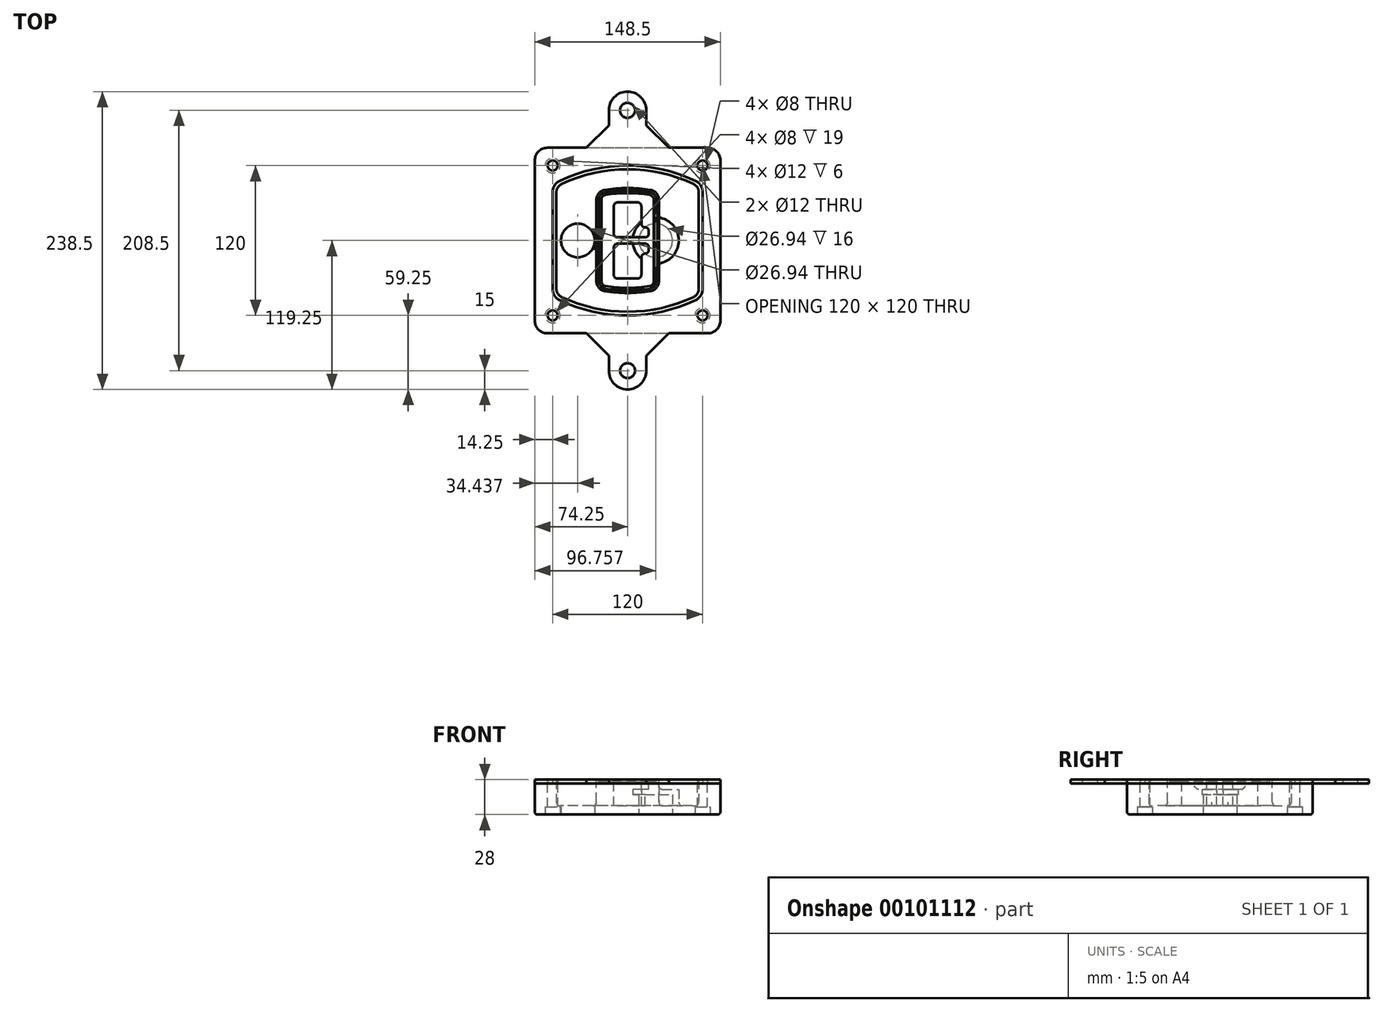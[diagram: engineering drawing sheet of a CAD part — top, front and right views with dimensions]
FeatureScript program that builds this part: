
annotation { "Feature Type Name" : "Feature", "Feature Type Description" : "" }
export const myFeature = defineFeature(function(context is Context, id is Id, definition is map)
    precondition{}
    {
        {
            var Q0;
            Q0=qCreatedBy(makeId("Top.planeOp"),FACE);
            var sketch = newSketch(context, id + "F0", { "sketchPlane" : qUnion([Q0])});
            skPoint(sketch, "E0.rect.middle", {"position": v(0, 0) * mm});
            skLineSegment(sketch, "E1.bottom", {"start": v(-64.25, -74.25) * mm, "end": v(64.25, -74.25) * mm});
            skLineSegment(sketch, "E1.top", {"start": v(-64.25, 74.25) * mm, "end": v(64.25, 74.25) * mm});
            skLineSegment(sketch, "E1.left", {"start": v(-74.25, -64.25) * mm, "end": v(-74.25, 64.25) * mm});
            skLineSegment(sketch, "E1.right", {"start": v(74.25, -64.25) * mm, "end": v(74.25, 64.25) * mm});
            skLineSegment(sketch, "E2", {"start": v(-74.25, 74.25) * mm, "end": v(74.25, -74.25) * mm, "construction": true});
            skLineSegment(sketch, "E3", {"start": v(74.25, 74.25) * mm, "end": v(-74.25, -74.25) * mm, "construction": true});
            skCircle(sketch, "E4", {"center": v(-60, 60) * mm, "radius": 4 * mm});
            skCircle(sketch, "E5", {"center": v(60, 60) * mm, "radius": 4 * mm});
            skCircle(sketch, "E6", {"center": v(60, -60) * mm, "radius": 4 * mm});
            skCircle(sketch, "E7", {"center": v(-60, -60) * mm, "radius": 4 * mm});
            skLineSegment(sketch, "E8", {"start": v(-60, 60) * mm, "end": v(60, 60) * mm, "construction": true});
            skLineSegment(sketch, "E9", {"start": v(60, 60) * mm, "end": v(60, -60) * mm, "construction": true});
            skLineSegment(sketch, "E10", {"start": v(60, -60) * mm, "end": v(-60, -60) * mm, "construction": true});
            skLineSegment(sketch, "E11", {"start": v(-60, -60) * mm, "end": v(-60, 60) * mm, "construction": true});
            skLineSegment(sketch, "E12", {"start": v(-60, 38.83) * mm, "end": v(-60, -38.83) * mm});
            skLineSegment(sketch, "E13", {"start": v(60, 38.83) * mm, "end": v(60, -38.83) * mm});
            skArc(sketch, "E14", {"start": v(54.26, 47.88) * mm, "mid": v(0, 60) * mm, "end": v(-54.26, 47.88) * mm});
            skArc(sketch, "E15", {"start": v(-54.26, -47.88) * mm, "mid": v(0, -60) * mm, "end": v(54.26, -47.88) * mm});
            skLineSegment(sketch, "E16", {"start": v(-60, 0) * mm, "end": v(60, 0) * mm, "construction": true});
            skPoint(sketch, "E17.visualSharp", {"position": v(-60, -45) * mm});
            skArc(sketch, "E17.filletArc", {"start": v(-60, -38.83) * mm, "mid": v(-58.44, -44.2) * mm, "end": v(-54.26, -47.88) * mm});
            skPoint(sketch, "E18.visualSharp", {"position": v(-60, 45) * mm});
            skArc(sketch, "E18.filletArc", {"start": v(-54.26, 47.88) * mm, "mid": v(-58.44, 44.2) * mm, "end": v(-60, 38.83) * mm});
            skPoint(sketch, "E19.visualSharp", {"position": v(60, 45) * mm});
            skArc(sketch, "E19.filletArc", {"start": v(60, 38.83) * mm, "mid": v(58.44, 44.2) * mm, "end": v(54.26, 47.88) * mm});
            skPoint(sketch, "E20.visualSharp", {"position": v(60, -45) * mm});
            skArc(sketch, "E20.filletArc", {"start": v(54.26, -47.88) * mm, "mid": v(58.44, -44.2) * mm, "end": v(60, -38.83) * mm});
            skPoint(sketch, "E21.visualSharp", {"position": v(-74.25, 74.25) * mm});
            skArc(sketch, "E21.filletArc", {"start": v(-64.25, 74.25) * mm, "mid": v(-71.32, 71.32) * mm, "end": v(-74.25, 64.25) * mm});
            skPoint(sketch, "E22.visualSharp", {"position": v(74.25, 74.25) * mm});
            skArc(sketch, "E22.filletArc", {"start": v(74.25, 64.25) * mm, "mid": v(71.32, 71.32) * mm, "end": v(64.25, 74.25) * mm});
            skPoint(sketch, "E23.visualSharp", {"position": v(74.25, -74.25) * mm});
            skArc(sketch, "E23.filletArc", {"start": v(64.25, -74.25) * mm, "mid": v(71.32, -71.32) * mm, "end": v(74.25, -64.25) * mm});
            skPoint(sketch, "E24.visualSharp", {"position": v(-74.25, -74.25) * mm});
            skArc(sketch, "E24.filletArc", {"start": v(-74.25, -64.25) * mm, "mid": v(-71.32, -71.32) * mm, "end": v(-64.25, -74.25) * mm});
            skArc(sketch, "E25.0", {"start": v(57, 38.83) * mm, "mid": v(55.9, 42.58) * mm, "end": v(52.98, 45.17) * mm});
            skLineSegment(sketch, "E25.1", {"start": v(57, 38.83) * mm, "end": v(57, -38.83) * mm});
            skArc(sketch, "E25.2", {"start": v(52.98, -45.17) * mm, "mid": v(55.9, -42.58) * mm, "end": v(57, -38.83) * mm});
            skArc(sketch, "E25.3", {"start": v(-52.98, -45.17) * mm, "mid": v(0, -57) * mm, "end": v(52.98, -45.17) * mm});
            skArc(sketch, "E25.4", {"start": v(-57, -38.83) * mm, "mid": v(-55.9, -42.58) * mm, "end": v(-52.98, -45.17) * mm});
            skArc(sketch, "E25.5", {"start": v(52.98, 45.17) * mm, "mid": v(0, 57) * mm, "end": v(-52.98, 45.17) * mm});
            skLineSegment(sketch, "E25.6", {"start": v(-57, 38.83) * mm, "end": v(-57, -38.83) * mm});
            skArc(sketch, "E25.7", {"start": v(-52.98, 45.17) * mm, "mid": v(-55.9, 42.58) * mm, "end": v(-57, 38.83) * mm});
            skArc(sketch, "E26.0", {"start": v(-55.96, 51.5) * mm, "mid": v(-61.82, 46.33) * mm, "end": v(-64, 38.83) * mm});
            skArc(sketch, "E26.1", {"start": v(55.96, 51.5) * mm, "mid": v(0, 64) * mm, "end": v(-55.96, 51.5) * mm});
            skArc(sketch, "E26.2", {"start": v(64, 38.83) * mm, "mid": v(61.82, 46.33) * mm, "end": v(55.96, 51.5) * mm});
            skLineSegment(sketch, "E26.3", {"start": v(64, 38.83) * mm, "end": v(64, -38.83) * mm});
            skArc(sketch, "E26.4", {"start": v(55.96, -51.5) * mm, "mid": v(61.82, -46.33) * mm, "end": v(64, -38.83) * mm});
            skLineSegment(sketch, "E26.5", {"start": v(-64, 38.83) * mm, "end": v(-64, -38.83) * mm});
            skArc(sketch, "E26.6", {"start": v(-55.96, -51.5) * mm, "mid": v(0, -64) * mm, "end": v(55.96, -51.5) * mm});
            skArc(sketch, "E26.7", {"start": v(-64, -38.83) * mm, "mid": v(-61.82, -46.33) * mm, "end": v(-55.96, -51.5) * mm});
            skSolve(sketch);
        }
        {
            var Q0;
            Q0=makeQuery(id+"F0.imprint","IMPRINT",FACE,{"disambiguationData":[TD([[makeQuery(id+"F0.imprint","IMPRINT",EDGE,{"derivedFrom":sQuery(id+"F0.wireOp",EDGE,"E1.bottom")}),1.0]])]});
            var Q1;
            Q1=makeQuery(id+"F0.imprint","IMPRINT",FACE,{"disambiguationData":[TD([[makeQuery(id+"F0.imprint","IMPRINT",EDGE,{"derivedFrom":sQuery(id+"F0.wireOp",EDGE,"E12")}),1.0]])]});
            var Q2;
            Q2=makeQuery(id+"F0.imprint","IMPRINT",FACE,{"disambiguationData":[TD([[makeQuery(id+"F0.imprint","IMPRINT",EDGE,{"derivedFrom":sQuery(id+"F0.wireOp",EDGE,"E25.0")}),1.0]])]});
            var Q3;
            Q3=makeQuery(id+"F0.imprint","IMPRINT",FACE,{"disambiguationData":[TD([[makeQuery(id+"F0.imprint","IMPRINT",EDGE,{"derivedFrom":sQuery(id+"F0.wireOp",EDGE,"E12")}),-1.0]])]});
            extrude(context, id + "F1", {"entities" : qUnion([Q0, Q1, Q2, Q3]), "oppositeDirection" : true, "depth" : 25 * mm});
        }
        {
            var Q0;
            Q0=makeQuery(id+"F0.imprint","IMPRINT",FACE,{"disambiguationData":[TD([[makeQuery(id+"F0.imprint","IMPRINT",EDGE,{"derivedFrom":sQuery(id+"F0.wireOp",EDGE,"E12")}),1.0]])]});
            extrude(context, id + "F2", {"entities" : qUnion([Q0]), "operationType" : NewBodyOperationType.ADD, "depth" : 3 * mm});
        }
        {
            var Q0;
            Q0=makeQuery(id+"F0.imprint","IMPRINT",FACE,{"disambiguationData":[TD([[makeQuery(id+"F0.imprint","IMPRINT",EDGE,{"derivedFrom":sQuery(id+"F0.wireOp",EDGE,"E25.0")}),1.0]])]});
            extrude(context, id + "F3", {"entities" : qUnion([Q0]), "operationType" : NewBodyOperationType.REMOVE, "oppositeDirection" : true, "depth" : 18 * mm});
        }
        {
            var Q0;
            Q0=makeQuery(id+"F2.opExtrude","CAP_FACE",FACE,{"disambiguationData":[OSD([sQuery(id+"F0.wireOp",EDGE,"E12"),sQuery(id+"F0.wireOp",EDGE,"E13"),sQuery(id+"F0.wireOp",EDGE,"E14"),sQuery(id+"F0.wireOp",EDGE,"E15"),sQuery(id+"F0.wireOp",EDGE,"E17.filletArc"),sQuery(id+"F0.wireOp",EDGE,"E18.filletArc"),sQuery(id+"F0.wireOp",EDGE,"E19.filletArc"),sQuery(id+"F0.wireOp",EDGE,"E20.filletArc"),sQuery(id+"F0.wireOp",EDGE,"E25.0"),sQuery(id+"F0.wireOp",EDGE,"E25.1"),sQuery(id+"F0.wireOp",EDGE,"E25.2"),sQuery(id+"F0.wireOp",EDGE,"E25.3"),sQuery(id+"F0.wireOp",EDGE,"E25.4"),sQuery(id+"F0.wireOp",EDGE,"E25.5"),sQuery(id+"F0.wireOp",EDGE,"E25.6"),sQuery(id+"F0.wireOp",EDGE,"E25.7")])],"isStart":false});
            var sketch = newSketch(context, id + "F4", { "sketchPlane" : qUnion([Q0])});
            skArc(sketch, "E27.0", {"start": v(-18.34, -40.45) * mm, "mid": v(0, -42) * mm, "end": v(18.34, -40.45) * mm});
            skArc(sketch, "E28.0", {"start": v(18.34, 40.45) * mm, "mid": v(0, 42) * mm, "end": v(-18.34, 40.45) * mm});
            skLineSegment(sketch, "E29", {"start": v(-25, 32.57) * mm, "end": v(-25, -32.57) * mm});
            skLineSegment(sketch, "E30", {"start": v(25, 32.57) * mm, "end": v(25, -32.57) * mm});
            skLineSegment(sketch, "E31", {"start": v(-25, 39.1) * mm, "end": v(25, 39.1) * mm, "construction": true});
            skLineSegment(sketch, "E32", {"start": v(-25, -39.1) * mm, "end": v(25, -39.1) * mm, "construction": true});
            skPoint(sketch, "E33.visualSharp", {"position": v(-25, 39.1) * mm});
            skArc(sketch, "E33.filletArc", {"start": v(-18.34, 40.45) * mm, "mid": v(-23.11, 37.73) * mm, "end": v(-25, 32.57) * mm});
            skPoint(sketch, "E34.visualSharp", {"position": v(25, 39.1) * mm});
            skArc(sketch, "E34.filletArc", {"start": v(25, 32.57) * mm, "mid": v(23.11, 37.73) * mm, "end": v(18.34, 40.45) * mm});
            skPoint(sketch, "E35.visualSharp", {"position": v(25, -39.1) * mm});
            skArc(sketch, "E35.filletArc", {"start": v(18.34, -40.45) * mm, "mid": v(23.11, -37.73) * mm, "end": v(25, -32.57) * mm});
            skPoint(sketch, "E36.visualSharp", {"position": v(-25, -39.1) * mm});
            skArc(sketch, "E36.filletArc", {"start": v(-25, -32.57) * mm, "mid": v(-23.11, -37.73) * mm, "end": v(-18.34, -40.45) * mm});
            skArc(sketch, "E37.0", {"start": v(52.98, 45.17) * mm, "mid": v(0, 57) * mm, "end": v(-52.98, 45.17) * mm});
            skArc(sketch, "E37.1", {"start": v(-52.98, 45.17) * mm, "mid": v(-55.9, 42.58) * mm, "end": v(-57, 38.83) * mm});
            skLineSegment(sketch, "E37.2", {"start": v(-57, 38.83) * mm, "end": v(-57, -38.83) * mm});
            skArc(sketch, "E37.3", {"start": v(-57, -38.83) * mm, "mid": v(-55.9, -42.58) * mm, "end": v(-52.98, -45.17) * mm});
            skArc(sketch, "E37.4", {"start": v(-52.98, -45.17) * mm, "mid": v(0, -57) * mm, "end": v(52.98, -45.17) * mm});
            skArc(sketch, "E37.5", {"start": v(52.98, -45.17) * mm, "mid": v(55.9, -42.58) * mm, "end": v(57, -38.83) * mm});
            skLineSegment(sketch, "E37.6", {"start": v(57, 38.83) * mm, "end": v(57, -38.83) * mm});
            skArc(sketch, "E37.7", {"start": v(57, 38.83) * mm, "mid": v(55.9, 42.58) * mm, "end": v(52.98, 45.17) * mm});
            skLineSegment(sketch, "E38.0", {"start": v(23, 32.57) * mm, "end": v(23, -32.57) * mm});
            skArc(sketch, "E38.1", {"start": v(18, -38.48) * mm, "mid": v(21.58, -36.44) * mm, "end": v(23, -32.57) * mm});
            skArc(sketch, "E38.2", {"start": v(-18, -38.48) * mm, "mid": v(0, -40) * mm, "end": v(18, -38.48) * mm});
            skArc(sketch, "E38.3", {"start": v(-23, -32.57) * mm, "mid": v(-21.58, -36.44) * mm, "end": v(-18, -38.48) * mm});
            skLineSegment(sketch, "E38.4", {"start": v(-23, 32.57) * mm, "end": v(-23, -32.57) * mm});
            skArc(sketch, "E38.5", {"start": v(23, 32.57) * mm, "mid": v(21.58, 36.44) * mm, "end": v(18, 38.48) * mm});
            skArc(sketch, "E38.6", {"start": v(-18, 38.48) * mm, "mid": v(-21.58, 36.44) * mm, "end": v(-23, 32.57) * mm});
            skArc(sketch, "E38.7", {"start": v(18, 38.48) * mm, "mid": v(0, 40) * mm, "end": v(-18, 38.48) * mm});
            skArc(sketch, "E39.0", {"start": v(21, 32.57) * mm, "mid": v(20.06, 35.15) * mm, "end": v(17.67, 36.5) * mm});
            skLineSegment(sketch, "E39.1", {"start": v(21, 32.57) * mm, "end": v(21, -32.57) * mm});
            skArc(sketch, "E39.2", {"start": v(17.67, -36.5) * mm, "mid": v(20.06, -35.15) * mm, "end": v(21, -32.57) * mm});
            skArc(sketch, "E39.3", {"start": v(-17.67, -36.5) * mm, "mid": v(0, -38) * mm, "end": v(17.67, -36.5) * mm});
            skArc(sketch, "E39.4", {"start": v(-21, -32.57) * mm, "mid": v(-20.06, -35.15) * mm, "end": v(-17.67, -36.5) * mm});
            skArc(sketch, "E39.5", {"start": v(17.67, 36.5) * mm, "mid": v(0, 38) * mm, "end": v(-17.67, 36.5) * mm});
            skLineSegment(sketch, "E39.6", {"start": v(-21, 32.57) * mm, "end": v(-21, -32.57) * mm});
            skArc(sketch, "E39.7", {"start": v(-17.67, 36.5) * mm, "mid": v(-20.06, 35.15) * mm, "end": v(-21, 32.57) * mm});
            skLineSegment(sketch, "E40", {"start": v(-25, 0) * mm, "end": v(25, 0) * mm, "construction": true});
            skLineSegment(sketch, "E41", {"start": v(-11, 5.5) * mm, "end": v(-11, 27.5) * mm});
            skLineSegment(sketch, "E42", {"start": v(-8, 30.5) * mm, "end": v(8, 30.5) * mm});
            skLineSegment(sketch, "E43", {"start": v(11, 27.5) * mm, "end": v(11, 13.5) * mm});
            skLineSegment(sketch, "E44", {"start": v(14, 10.5) * mm, "end": v(14, 10.5) * mm});
            skLineSegment(sketch, "E45", {"start": v(17, 7.5) * mm, "end": v(17, 5.5) * mm});
            skLineSegment(sketch, "E46", {"start": v(14, 2.5) * mm, "end": v(-8, 2.5) * mm});
            skPoint(sketch, "E47.visualSharp", {"position": v(-11, 30.5) * mm});
            skArc(sketch, "E47.filletArc", {"start": v(-8, 30.5) * mm, "mid": v(-10.12, 29.62) * mm, "end": v(-11, 27.5) * mm});
            skPoint(sketch, "E48.visualSharp", {"position": v(11, 30.5) * mm});
            skArc(sketch, "E48.filletArc", {"start": v(11, 27.5) * mm, "mid": v(10.12, 29.62) * mm, "end": v(8, 30.5) * mm});
            skPoint(sketch, "E49.visualSharp", {"position": v(11, 10.5) * mm});
            skArc(sketch, "E49.filletArc", {"start": v(11, 13.5) * mm, "mid": v(11.88, 11.38) * mm, "end": v(14, 10.5) * mm});
            skPoint(sketch, "E50.visualSharp", {"position": v(17, 10.5) * mm});
            skArc(sketch, "E50.filletArc", {"start": v(17, 7.5) * mm, "mid": v(16.12, 9.62) * mm, "end": v(14, 10.5) * mm});
            skPoint(sketch, "E51.visualSharp", {"position": v(17, 2.5) * mm});
            skArc(sketch, "E51.filletArc", {"start": v(14, 2.5) * mm, "mid": v(16.12, 3.38) * mm, "end": v(17, 5.5) * mm});
            skPoint(sketch, "E52.visualSharp", {"position": v(-11, 2.5) * mm});
            skArc(sketch, "E52.filletArc", {"start": v(-11, 5.5) * mm, "mid": v(-10.12, 3.38) * mm, "end": v(-8, 2.5) * mm});
            skLineSegment(sketch, "E53.0.MirrorCS", {"start": v(14, -2.5) * mm, "end": v(-8, -2.5) * mm});
            skArc(sketch, "E54.0.MirrorCS", {"start": v(-11, -5.5) * mm, "mid": v(-10.12, -3.38) * mm, "end": v(-8, -2.5) * mm});
            skLineSegment(sketch, "E55.0.MirrorCS", {"start": v(-11, -5.5) * mm, "end": v(-11, -27.5) * mm});
            skArc(sketch, "E56.0.MirrorCS", {"start": v(-8, -30.5) * mm, "mid": v(-10.12, -29.62) * mm, "end": v(-11, -27.5) * mm});
            skLineSegment(sketch, "E57.0.MirrorCS", {"start": v(-8, -30.5) * mm, "end": v(8, -30.5) * mm});
            skArc(sketch, "E58.0.MirrorCS", {"start": v(11, -27.5) * mm, "mid": v(10.12, -29.62) * mm, "end": v(8, -30.5) * mm});
            skLineSegment(sketch, "E59.0.MirrorCS", {"start": v(11, -27.5) * mm, "end": v(11, -13.5) * mm});
            skArc(sketch, "E60.0.MirrorCS", {"start": v(11, -13.5) * mm, "mid": v(11.88, -11.38) * mm, "end": v(14, -10.5) * mm});
            skArc(sketch, "E61.0.MirrorCS", {"start": v(17, -7.5) * mm, "mid": v(16.12, -9.62) * mm, "end": v(14, -10.5) * mm});
            skLineSegment(sketch, "E62.0.MirrorCS", {"start": v(17, -7.5) * mm, "end": v(17, -5.5) * mm});
            skArc(sketch, "E63.0.MirrorCS", {"start": v(14, -2.5) * mm, "mid": v(16.12, -3.38) * mm, "end": v(17, -5.5) * mm});
            skSolve(sketch);
        }
        {
            var Q0;
            Q0=makeQuery(id+"F4.imprint","IMPRINT",FACE,{"disambiguationData":[TD([[makeQuery(id+"F4.imprint","IMPRINT",EDGE,{"derivedFrom":sQuery(id+"F4.wireOp",EDGE,"E27.0")}),1.0]])]});
            var Q1;
            Q1=makeQuery(id+"F4.imprint","IMPRINT",FACE,{"disambiguationData":[TD([[makeQuery(id+"F4.imprint","IMPRINT",EDGE,{"derivedFrom":sQuery(id+"F4.wireOp",EDGE,"E38.0")}),-1.0]])]});
            var Q2;
            Q2=makeQuery(id+"F4.imprint","IMPRINT",FACE,{"disambiguationData":[TD([[makeQuery(id+"F4.imprint","IMPRINT",EDGE,{"derivedFrom":sQuery(id+"F4.wireOp",EDGE,"E39.0")}),1.0]])]});
            extrude(context, id + "F5", {"entities" : qUnion([Q0, Q1, Q2]), "operationType" : NewBodyOperationType.ADD, "endBound" : BoundingType.UP_TO_NEXT, "oppositeDirection" : true, "depth" : 25 * mm});
        }
        {
            var Q0;
            Q0=makeQuery(id+"F4.imprint","IMPRINT",FACE,{"disambiguationData":[TD([[makeQuery(id+"F4.imprint","IMPRINT",EDGE,{"derivedFrom":sQuery(id+"F4.wireOp",EDGE,"E38.0")}),-1.0]])]});
            extrude(context, id + "F6", {"entities" : qUnion([Q0]), "operationType" : NewBodyOperationType.REMOVE, "oppositeDirection" : true, "depth" : 2 * mm});
        }
        {
            var Q0;
            Q0=makeQuery(id+"F1.opExtrude","CAP_FACE",FACE,{"disambiguationData":[OSD([sQuery(id+"F0.wireOp",EDGE,"E1.bottom"),sQuery(id+"F0.wireOp",EDGE,"E1.top"),sQuery(id+"F0.wireOp",EDGE,"E1.left"),sQuery(id+"F0.wireOp",EDGE,"E1.right"),sQuery(id+"F0.wireOp",EDGE,"E4"),sQuery(id+"F0.wireOp",EDGE,"E5"),sQuery(id+"F0.wireOp",EDGE,"E6"),sQuery(id+"F0.wireOp",EDGE,"E7"),sQuery(id+"F0.wireOp",EDGE,"E21.filletArc"),sQuery(id+"F0.wireOp",EDGE,"E22.filletArc"),sQuery(id+"F0.wireOp",EDGE,"E23.filletArc"),sQuery(id+"F0.wireOp",EDGE,"E24.filletArc")])],"isStart":false});
            var sketch = newSketch(context, id + "F7", { "sketchPlane" : qUnion([Q0])});
            skCircle(sketch, "E64", {"center": v(22.5, 0) * mm, "radius": 13.47 * mm});
            skCircle(sketch, "E65", {"center": v(-39.81, 0) * mm, "radius": 13.47 * mm});
            skLineSegment(sketch, "E66", {"start": v(74.25, 0) * mm, "end": v(-74.25, 0) * mm});
            skCircle(sketch, "E67", {"center": v(22.5, 0) * mm, "radius": 18.47 * mm});
            skCircle(sketch, "E68", {"center": v(60, -60) * mm, "radius": 6 * mm});
            skCircle(sketch, "E69", {"center": v(-60, -60) * mm, "radius": 6 * mm});
            skCircle(sketch, "E70", {"center": v(-60, 60) * mm, "radius": 6 * mm});
            skCircle(sketch, "E71", {"center": v(60, 60) * mm, "radius": 6 * mm});
            skSolve(sketch);
        }
        {
            var Q0;
            {var subQ1=sQuery(id+"F7.wireOp",EDGE,"E66");var subQ4=sQuery(id+"F7.wireOp",EDGE,"E64");var subQ6=makeQuery(id+"F7.imprint","INTERSECT",VERTEX,{"disambiguationData":[OD(0.0)],"derivedFrom":[subQ4,subQ1]});Q0=makeQuery(id+"F7.imprint","IMPRINT",FACE,{"disambiguationData":[TD([[makeQuery(id+"F7.imprint","IMPRINT",EDGE,{"disambiguationData":[TD([[subQ6,-1.0]])],"derivedFrom":subQ4}),-1.0]])]});}
            var Q1;
            {var subQ0=sQuery(id+"F7.wireOp",EDGE,"E66");var subQ1=sQuery(id+"F7.wireOp",EDGE,"E64");var subQ3=makeQuery(id+"F7.imprint","INTERSECT",VERTEX,{"disambiguationData":[OD(0.0)],"derivedFrom":[subQ1,subQ0]});Q1=makeQuery(id+"F7.imprint","IMPRINT",FACE,{"disambiguationData":[TD([[makeQuery(id+"F7.imprint","IMPRINT",EDGE,{"disambiguationData":[TD([[subQ3,-1.0]])],"derivedFrom":subQ1}),1.0]])]});}
            var Q2;
            {var subQ0=sQuery(id+"F7.wireOp",EDGE,"E66");var subQ1=sQuery(id+"F7.wireOp",EDGE,"E64");var subQ3=makeQuery(id+"F7.imprint","INTERSECT",VERTEX,{"disambiguationData":[OD(0.0)],"derivedFrom":[subQ1,subQ0]});Q2=makeQuery(id+"F7.imprint","IMPRINT",FACE,{"disambiguationData":[TD([[makeQuery(id+"F7.imprint","IMPRINT",EDGE,{"disambiguationData":[TD([[subQ3,1.0]])],"derivedFrom":subQ1}),1.0]])]});}
            var Q3;
            {var subQ1=sQuery(id+"F7.wireOp",EDGE,"E66");var subQ4=sQuery(id+"F7.wireOp",EDGE,"E64");var subQ6=makeQuery(id+"F7.imprint","INTERSECT",VERTEX,{"disambiguationData":[OD(0.0)],"derivedFrom":[subQ4,subQ1]});Q3=makeQuery(id+"F7.imprint","IMPRINT",FACE,{"disambiguationData":[TD([[makeQuery(id+"F7.imprint","IMPRINT",EDGE,{"disambiguationData":[TD([[subQ6,1.0]])],"derivedFrom":subQ4}),-1.0]])]});}
            extrude(context, id + "F8", {"entities" : qUnion([Q0, Q1, Q2, Q3]), "operationType" : NewBodyOperationType.ADD, "oppositeDirection" : true, "depth" : 20 * mm});
        }
        {
            var Q0;
            {var subQ0=sQuery(id+"F7.wireOp",EDGE,"E66");var subQ1=sQuery(id+"F7.wireOp",EDGE,"E64");var subQ3=makeQuery(id+"F7.imprint","INTERSECT",VERTEX,{"disambiguationData":[OD(0.0)],"derivedFrom":[subQ1,subQ0]});Q0=makeQuery(id+"F7.imprint","IMPRINT",FACE,{"disambiguationData":[TD([[makeQuery(id+"F7.imprint","IMPRINT",EDGE,{"disambiguationData":[TD([[subQ3,-1.0]])],"derivedFrom":subQ1}),1.0]])]});}
            var Q1;
            {var subQ0=sQuery(id+"F7.wireOp",EDGE,"E66");var subQ1=sQuery(id+"F7.wireOp",EDGE,"E64");var subQ3=makeQuery(id+"F7.imprint","INTERSECT",VERTEX,{"disambiguationData":[OD(0.0)],"derivedFrom":[subQ1,subQ0]});Q1=makeQuery(id+"F7.imprint","IMPRINT",FACE,{"disambiguationData":[TD([[makeQuery(id+"F7.imprint","IMPRINT",EDGE,{"disambiguationData":[TD([[subQ3,1.0]])],"derivedFrom":subQ1}),1.0]])]});}
            extrude(context, id + "F9", {"entities" : qUnion([Q0, Q1]), "operationType" : NewBodyOperationType.REMOVE, "oppositeDirection" : true, "depth" : 16 * mm});
        }
        {
            var Q0;
            {var subQ0=sQuery(id+"F7.wireOp",EDGE,"E66");var subQ1=sQuery(id+"F7.wireOp",EDGE,"E65");var subQ3=makeQuery(id+"F7.imprint","INTERSECT",VERTEX,{"disambiguationData":[OD(0.0)],"derivedFrom":[subQ1,subQ0]});Q0=makeQuery(id+"F7.imprint","IMPRINT",FACE,{"disambiguationData":[TD([[makeQuery(id+"F7.imprint","IMPRINT",EDGE,{"disambiguationData":[TD([[subQ3,-1.0]])],"derivedFrom":subQ1}),1.0]])]});}
            var Q1;
            {var subQ0=sQuery(id+"F7.wireOp",EDGE,"E66");var subQ1=sQuery(id+"F7.wireOp",EDGE,"E65");var subQ3=makeQuery(id+"F7.imprint","INTERSECT",VERTEX,{"disambiguationData":[OD(0.0)],"derivedFrom":[subQ1,subQ0]});Q1=makeQuery(id+"F7.imprint","IMPRINT",FACE,{"disambiguationData":[TD([[makeQuery(id+"F7.imprint","IMPRINT",EDGE,{"disambiguationData":[TD([[subQ3,1.0]])],"derivedFrom":subQ1}),1.0]])]});}
            extrude(context, id + "F10", {"entities" : qUnion([Q0, Q1]), "operationType" : NewBodyOperationType.REMOVE, "oppositeDirection" : true, "depth" : 25 * mm});
        }
        {
            var Q0;
            Q0=makeQuery(id+"F7.imprint","IMPRINT",FACE,{"disambiguationData":[TD([[makeQuery(id+"F7.imprint","IMPRINT",EDGE,{"derivedFrom":sQuery(id+"F7.wireOp",EDGE,"E68")}),1.0]])]});
            var Q1;
            Q1=makeQuery(id+"F7.imprint","IMPRINT",FACE,{"disambiguationData":[TD([[makeQuery(id+"F7.imprint","IMPRINT",EDGE,{"derivedFrom":makeQuery(id+"F1.opExtrude","CAP_EDGE",EDGE,{"disambiguationData":[OSD([sQuery(id+"F0.wireOp",EDGE,"E5")])],"isStart":false})}),-1.0]])]});
            var Q2;
            Q2=makeQuery(id+"F7.imprint","IMPRINT",FACE,{"disambiguationData":[TD([[makeQuery(id+"F7.imprint","IMPRINT",EDGE,{"derivedFrom":sQuery(id+"F7.wireOp",EDGE,"E69")}),1.0]])]});
            var Q3;
            Q3=makeQuery(id+"F7.imprint","IMPRINT",FACE,{"disambiguationData":[TD([[makeQuery(id+"F7.imprint","IMPRINT",EDGE,{"derivedFrom":makeQuery(id+"F1.opExtrude","CAP_EDGE",EDGE,{"disambiguationData":[OSD([sQuery(id+"F0.wireOp",EDGE,"E4")])],"isStart":false})}),-1.0]])]});
            var Q4;
            Q4=makeQuery(id+"F7.imprint","IMPRINT",FACE,{"disambiguationData":[TD([[makeQuery(id+"F7.imprint","IMPRINT",EDGE,{"derivedFrom":sQuery(id+"F7.wireOp",EDGE,"E70")}),1.0]])]});
            var Q5;
            Q5=makeQuery(id+"F7.imprint","IMPRINT",FACE,{"disambiguationData":[TD([[makeQuery(id+"F7.imprint","IMPRINT",EDGE,{"derivedFrom":makeQuery(id+"F1.opExtrude","CAP_EDGE",EDGE,{"disambiguationData":[OSD([sQuery(id+"F0.wireOp",EDGE,"E7")])],"isStart":false})}),-1.0]])]});
            var Q6;
            Q6=makeQuery(id+"F7.imprint","IMPRINT",FACE,{"disambiguationData":[TD([[makeQuery(id+"F7.imprint","IMPRINT",EDGE,{"derivedFrom":sQuery(id+"F7.wireOp",EDGE,"E71")}),1.0]])]});
            var Q7;
            Q7=makeQuery(id+"F7.imprint","IMPRINT",FACE,{"disambiguationData":[TD([[makeQuery(id+"F7.imprint","IMPRINT",EDGE,{"derivedFrom":makeQuery(id+"F1.opExtrude","CAP_EDGE",EDGE,{"disambiguationData":[OSD([sQuery(id+"F0.wireOp",EDGE,"E6")])],"isStart":false})}),-1.0]])]});
            extrude(context, id + "F11", {"entities" : qUnion([Q0, Q1, Q2, Q3, Q4, Q5, Q6, Q7]), "operationType" : NewBodyOperationType.REMOVE, "oppositeDirection" : true, "depth" : 6 * mm});
        }
        {
            var Q0;
            Q0=makeQuery(id+"F9.boolean.opBoolean","COPY",FACE,{"derivedFrom":makeQuery(id+"F9.opExtrude","CAP_FACE",FACE,{"disambiguationData":[OSD([sQuery(id+"F7.wireOp",EDGE,"E64")])],"isStart":false})});
            var sketch = newSketch(context, id + "F12", { "sketchPlane" : qUnion([Q0])});
            skArc(sketch, "E72.0", {"start": v(11, 14.45) * mm, "mid": v(6.45, 9.13) * mm, "end": v(4.2, 2.5) * mm});
            skArc(sketch, "E72.1", {"start": v(4.2, -2.5) * mm, "mid": v(6.45, -9.13) * mm, "end": v(11, -14.45) * mm});
            skLineSegment(sketch, "E73", {"start": v(4.2, -2.5) * mm, "end": v(14, -2.5) * mm});
            skLineSegment(sketch, "E74.0", {"start": v(14, 2.5) * mm, "end": v(4.2, 2.5) * mm});
            skArc(sketch, "E74.1", {"start": v(14, 2.5) * mm, "mid": v(16.12, 3.38) * mm, "end": v(17, 5.5) * mm});
            skLineSegment(sketch, "E74.2", {"start": v(17, 7.5) * mm, "end": v(17, 5.5) * mm});
            skArc(sketch, "E74.3", {"start": v(17, 7.5) * mm, "mid": v(16.12, 9.62) * mm, "end": v(14, 10.5) * mm});
            skArc(sketch, "E74.4", {"start": v(11, 13.5) * mm, "mid": v(11.88, 11.38) * mm, "end": v(14, 10.5) * mm});
            skLineSegment(sketch, "E74.5", {"start": v(11, 14.45) * mm, "end": v(11, 13.5) * mm});
            skLineSegment(sketch, "E74.7", {"start": v(14, -2.5) * mm, "end": v(4.2, -2.5) * mm});
            skArc(sketch, "E74.8", {"start": v(14, -2.5) * mm, "mid": v(16.12, -3.38) * mm, "end": v(17, -5.5) * mm});
            skLineSegment(sketch, "E74.9", {"start": v(17, -7.5) * mm, "end": v(17, -5.5) * mm});
            skArc(sketch, "E74.10", {"start": v(17, -7.5) * mm, "mid": v(16.12, -9.62) * mm, "end": v(14, -10.5) * mm});
            skArc(sketch, "E74.11", {"start": v(11, -13.5) * mm, "mid": v(11.88, -11.38) * mm, "end": v(14, -10.5) * mm});
            skLineSegment(sketch, "E74.12", {"start": v(11, -14.45) * mm, "end": v(11, -13.5) * mm});
            skPoint(sketch, "E75.orphan", {"position": v(11, -27.5) * mm});
            skPoint(sketch, "E76.orphan", {"position": v(-8, -2.5) * mm});
            skPoint(sketch, "E77.orphan", {"position": v(-8, 2.5) * mm});
            skPoint(sketch, "E78.orphan", {"position": v(11, 27.5) * mm});
            skSolve(sketch);
        }
        {
            var Q0;
            {var subQ7=sQuery(id+"F12.wireOp",EDGE,"E72.0");var subQ14=sQuery(id+"F12.wireOp",EDGE,"E72.1");var subQ16=sQuery(id+"F12.wireOp",EDGE,"E74.1");var subQ18=sQuery(id+"F12.wireOp",EDGE,"E74.8");Q0=qUnion([makeQuery(id+"F12.imprint","IMPRINT",FACE,{"disambiguationData":[TD([[makeQuery(id+"F12.imprint","IMPRINT",EDGE,{"derivedFrom":subQ7}),1.0]])]}),makeQuery(id+"F12.imprint","IMPRINT",FACE,{"disambiguationData":[TD([[makeQuery(id+"F12.imprint","IMPRINT",EDGE,{"derivedFrom":subQ14}),1.0]])]}),makeQuery(id+"F12.imprint","IMPRINT",FACE,{"disambiguationData":[TD([[makeQuery(id+"F12.imprint","IMPRINT",EDGE,{"derivedFrom":subQ16}),1.0]])]}),makeQuery(id+"F12.imprint","IMPRINT",FACE,{"disambiguationData":[TD([[makeQuery(id+"F12.imprint","IMPRINT",EDGE,{"derivedFrom":subQ18}),-1.0]])]})]);}
            var Q1;
            Q1=makeQuery(id+"F5.boolean.opBoolean","SPLIT",FACE,{"disambiguationData":[TD([makeQuery(id+"F5.opExtrude","SWEPT_FACE",FACE,{"disambiguationData":[OSD([sQuery(id+"F4.wireOp",EDGE,"E41")])]})])],"derivedFrom":makeQuery(id+"F3.boolean.opBoolean","COPY",FACE,{"derivedFrom":makeQuery(id+"F3.opExtrude","CAP_FACE",FACE,{"disambiguationData":[OSD([sQuery(id+"F0.wireOp",EDGE,"E25.0"),sQuery(id+"F0.wireOp",EDGE,"E25.1"),sQuery(id+"F0.wireOp",EDGE,"E25.2"),sQuery(id+"F0.wireOp",EDGE,"E25.3"),sQuery(id+"F0.wireOp",EDGE,"E25.4"),sQuery(id+"F0.wireOp",EDGE,"E25.5"),sQuery(id+"F0.wireOp",EDGE,"E25.6"),sQuery(id+"F0.wireOp",EDGE,"E25.7")])],"isStart":false})})});
            extrude(context, id + "F13", {"entities" : qUnion([Q0]), "operationType" : NewBodyOperationType.REMOVE, "endBound" : BoundingType.UP_TO_SURFACE, "endBoundEntityFace" : qUnion([Q1]), "depth" : 25 * mm});
        }
        {
            var Q0;
            Q0=makeQuery(id+"F3.boolean.opBoolean","COPY",EDGE,{"derivedFrom":makeQuery(id+"F3.opExtrude","CAP_EDGE",EDGE,{"disambiguationData":[OSD([sQuery(id+"F0.wireOp",EDGE,"E25.6")])],"isStart":false})});
            var Q1;
            Q1=makeQuery(id+"F8.boolean.opBoolean","INTERSECT",EDGE,{"derivedFrom":[makeQuery(id+"F5.opExtrude","SWEPT_FACE",FACE,{"disambiguationData":[OSD([sQuery(id+"F4.wireOp",EDGE,"E30")])]}),makeQuery(id+"F8.opExtrude","CAP_FACE",FACE,{"disambiguationData":[OSD([sQuery(id+"F7.wireOp",EDGE,"E67")])],"isStart":false})]});
            var Q2;
            Q2=makeQuery(id+"F8.boolean.opBoolean","INTERSECT",EDGE,{"disambiguationData":[OD(1.0)],"derivedFrom":[makeQuery(id+"F5.opExtrude","SWEPT_FACE",FACE,{"disambiguationData":[OSD([sQuery(id+"F4.wireOp",EDGE,"E30")])]}),makeQuery(id+"F8.opExtrude","SWEPT_FACE",FACE,{"disambiguationData":[OSD([sQuery(id+"F7.wireOp",EDGE,"E67")])]})]});
            var Q3;
            {var subQ0=sQuery(id+"F4.wireOp",EDGE,"E30");Q3=makeQuery(id+"F8.boolean.opBoolean","SPLIT",EDGE,{"disambiguationData":[TD([makeQuery(id+"F5.opExtrude","SWEPT_FACE",FACE,{"disambiguationData":[OSD([sQuery(id+"F4.wireOp",EDGE,"E35.filletArc")])]})])],"derivedFrom":makeQuery(id+"F5.opExtrude","CAP_EDGE",EDGE,{"disambiguationData":[OSD([subQ0])],"isStart":false})});}
            var Q4;
            {var subQ0=sQuery(id+"F0.wireOp",EDGE,"E25.7");var subQ1=sQuery(id+"F0.wireOp",EDGE,"E25.1");var subQ2=sQuery(id+"F0.wireOp",EDGE,"E25.6");var subQ3=sQuery(id+"F0.wireOp",EDGE,"E25.5");var subQ4=sQuery(id+"F0.wireOp",EDGE,"E25.4");var subQ5=sQuery(id+"F0.wireOp",EDGE,"E25.0");var subQ6=sQuery(id+"F0.wireOp",EDGE,"E25.2");var subQ7=sQuery(id+"F0.wireOp",EDGE,"E25.3");Q4=makeQuery(id+"F8.boolean.opBoolean","INTERSECT",EDGE,{"derivedFrom":[makeQuery(id+"F5.boolean.opBoolean","SPLIT",FACE,{"disambiguationData":[TD([makeQuery(id+"F2.opExtrude","SWEPT_FACE",FACE,{"disambiguationData":[OSD([subQ5])]})])],"derivedFrom":makeQuery(id+"F3.boolean.opBoolean","COPY",FACE,{"derivedFrom":makeQuery(id+"F3.opExtrude","CAP_FACE",FACE,{"disambiguationData":[OSD([subQ5,subQ1,subQ6,subQ7,subQ4,subQ3,subQ2,subQ0])],"isStart":false})})}),makeQuery(id+"F8.opExtrude","SWEPT_FACE",FACE,{"disambiguationData":[OSD([sQuery(id+"F7.wireOp",EDGE,"E67")])]})]});}
            var Q5;
            Q5=makeQuery(id+"F8.boolean.opBoolean","INTERSECT",EDGE,{"disambiguationData":[OD(0.0)],"derivedFrom":[makeQuery(id+"F5.opExtrude","SWEPT_FACE",FACE,{"disambiguationData":[OSD([sQuery(id+"F4.wireOp",EDGE,"E30")])]}),makeQuery(id+"F8.opExtrude","SWEPT_FACE",FACE,{"disambiguationData":[OSD([sQuery(id+"F7.wireOp",EDGE,"E67")])]})]});
            fillet(context, id + "F14", {"entities" : qUnion([Q0, Q1, Q2, Q3, Q4, Q5]), "radius" : 3 * mm, "tangentPropagation" : true, "allowEdgeOverflow" : false});
        }
        {
            var Q0;
            Q0=makeQuery(id+"F1.opExtrude","CAP_EDGE",EDGE,{"disambiguationData":[OSD([sQuery(id+"F0.wireOp",EDGE,"E1.bottom")])],"isStart":false});
            fillet(context, id + "F15", {"entities" : qUnion([Q0]), "radius" : 2 * mm, "tangentPropagation" : true, "allowEdgeOverflow" : false});
        }
        {
            var Q0;
            {var subQ0=sQuery(id+"F0.wireOp",EDGE,"E22.filletArc");var subQ1=sQuery(id+"F0.wireOp",EDGE,"E7");var subQ2=sQuery(id+"F0.wireOp",EDGE,"E6");var subQ3=sQuery(id+"F0.wireOp",EDGE,"E5");var subQ4=sQuery(id+"F0.wireOp",EDGE,"E4");var subQ5=sQuery(id+"F0.wireOp",EDGE,"E1.bottom");var subQ6=sQuery(id+"F0.wireOp",EDGE,"E21.filletArc");var subQ7=sQuery(id+"F0.wireOp",EDGE,"E1.top");var subQ8=sQuery(id+"F0.wireOp",EDGE,"E1.left");var subQ9=sQuery(id+"F0.wireOp",EDGE,"E1.right");var subQ10=sQuery(id+"F0.wireOp",EDGE,"E23.filletArc");var subQ11=sQuery(id+"F0.wireOp",EDGE,"E24.filletArc");Q0=makeQuery(id+"F2.boolean.opBoolean","SPLIT",FACE,{"disambiguationData":[TD([makeQuery(id+"F1.opExtrude","SWEPT_FACE",FACE,{"disambiguationData":[OSD([subQ5])]})])],"derivedFrom":makeQuery(id+"F1.opExtrude","CAP_FACE",FACE,{"disambiguationData":[OSD([subQ5,subQ7,subQ8,subQ9,subQ4,subQ3,subQ2,subQ1,subQ6,subQ0,subQ10,subQ11])],"isStart":true})});}
            var sketch = newSketch(context, id + "F16", { "sketchPlane" : qUnion([Q0])});
            skLineSegment(sketch, "E79", {"start": v(0, 74.25) * mm, "end": v(0, 104.25) * mm, "construction": true});
            skLineSegment(sketch, "E80", {"start": v(-33, 74.25) * mm, "end": v(-15, 92.25) * mm});
            skLineSegment(sketch, "E81", {"start": v(-15, 92.25) * mm, "end": v(-15, 104.25) * mm});
            skArc(sketch, "E82", {"start": v(15, 104.25) * mm, "mid": v(0, 119.25) * mm, "end": v(-15, 104.25) * mm});
            skLineSegment(sketch, "E83", {"start": v(15, 104.25) * mm, "end": v(15, 92.25) * mm});
            skLineSegment(sketch, "E84", {"start": v(15, 92.25) * mm, "end": v(33, 74.25) * mm});
            skCircle(sketch, "E85", {"center": v(0, 104.25) * mm, "radius": 6 * mm});
            skLineSegment(sketch, "E86", {"start": v(-74.25, 0) * mm, "end": v(74.25, 0) * mm, "construction": true});
            skLineSegment(sketch, "E87.MirrorCS", {"start": v(-33, -74.25) * mm, "end": v(-15, -92.25) * mm});
            skLineSegment(sketch, "E88.MirrorCS", {"start": v(0, -74.25) * mm, "end": v(0, -104.25) * mm, "construction": true});
            skCircle(sketch, "E89.MirrorC", {"center": v(0, -104.25) * mm, "radius": 6 * mm});
            skLineSegment(sketch, "E90.MirrorCS", {"start": v(15, -92.25) * mm, "end": v(33, -74.25) * mm});
            skLineSegment(sketch, "E91.MirrorCS", {"start": v(15, -104.25) * mm, "end": v(15, -92.25) * mm});
            skLineSegment(sketch, "E92.MirrorCS", {"start": v(-15, -92.25) * mm, "end": v(-15, -104.25) * mm});
            skArc(sketch, "E93.MirrorCS", {"start": v(15, -104.25) * mm, "mid": v(0, -119.25) * mm, "end": v(-15, -104.25) * mm});
            skSolve(sketch);
        }
        {
            var Q0;
            {var subQ0=sQuery(id+"F16.wireOp",EDGE,"E87.MirrorCS");Q0=makeQuery(id+"F16.imprint","IMPRINT",FACE,{"disambiguationData":[TD([[makeQuery(id+"F16.imprint","IMPRINT",EDGE,{"derivedFrom":subQ0}),1.0]])]});}
            var Q1;
            {var subQ0=sQuery(id+"F16.wireOp",EDGE,"E80");Q1=makeQuery(id+"F16.imprint","IMPRINT",FACE,{"disambiguationData":[TD([[makeQuery(id+"F16.imprint","IMPRINT",EDGE,{"derivedFrom":subQ0}),-1.0]])]});}
            var Q2;
            Q2=makeQuery(id+"F16.imprint","IMPRINT",FACE,{"disambiguationData":[TD([[makeQuery(id+"F16.imprint","IMPRINT",EDGE,{"derivedFrom":makeQuery(id+"F1.opExtrude","CAP_EDGE",EDGE,{"disambiguationData":[OSD([sQuery(id+"F0.wireOp",EDGE,"E1.left")])],"isStart":true})}),-1.0]])]});
            var Q3;
            Q3=makeQuery(id+"F2.opExtrude","CAP_FACE",FACE,{"disambiguationData":[OSD([sQuery(id+"F0.wireOp",EDGE,"E12"),sQuery(id+"F0.wireOp",EDGE,"E13"),sQuery(id+"F0.wireOp",EDGE,"E14"),sQuery(id+"F0.wireOp",EDGE,"E15"),sQuery(id+"F0.wireOp",EDGE,"E17.filletArc"),sQuery(id+"F0.wireOp",EDGE,"E18.filletArc"),sQuery(id+"F0.wireOp",EDGE,"E19.filletArc"),sQuery(id+"F0.wireOp",EDGE,"E20.filletArc"),sQuery(id+"F0.wireOp",EDGE,"E25.0"),sQuery(id+"F0.wireOp",EDGE,"E25.1"),sQuery(id+"F0.wireOp",EDGE,"E25.2"),sQuery(id+"F0.wireOp",EDGE,"E25.3"),sQuery(id+"F0.wireOp",EDGE,"E25.4"),sQuery(id+"F0.wireOp",EDGE,"E25.5"),sQuery(id+"F0.wireOp",EDGE,"E25.6"),sQuery(id+"F0.wireOp",EDGE,"E25.7")])],"isStart":false});
            extrude(context, id + "F17", {"entities" : qUnion([Q0, Q1, Q2]), "endBound" : BoundingType.UP_TO_SURFACE, "endBoundEntityFace" : qUnion([Q3]), "depth" : 25 * mm});
        }
    });
